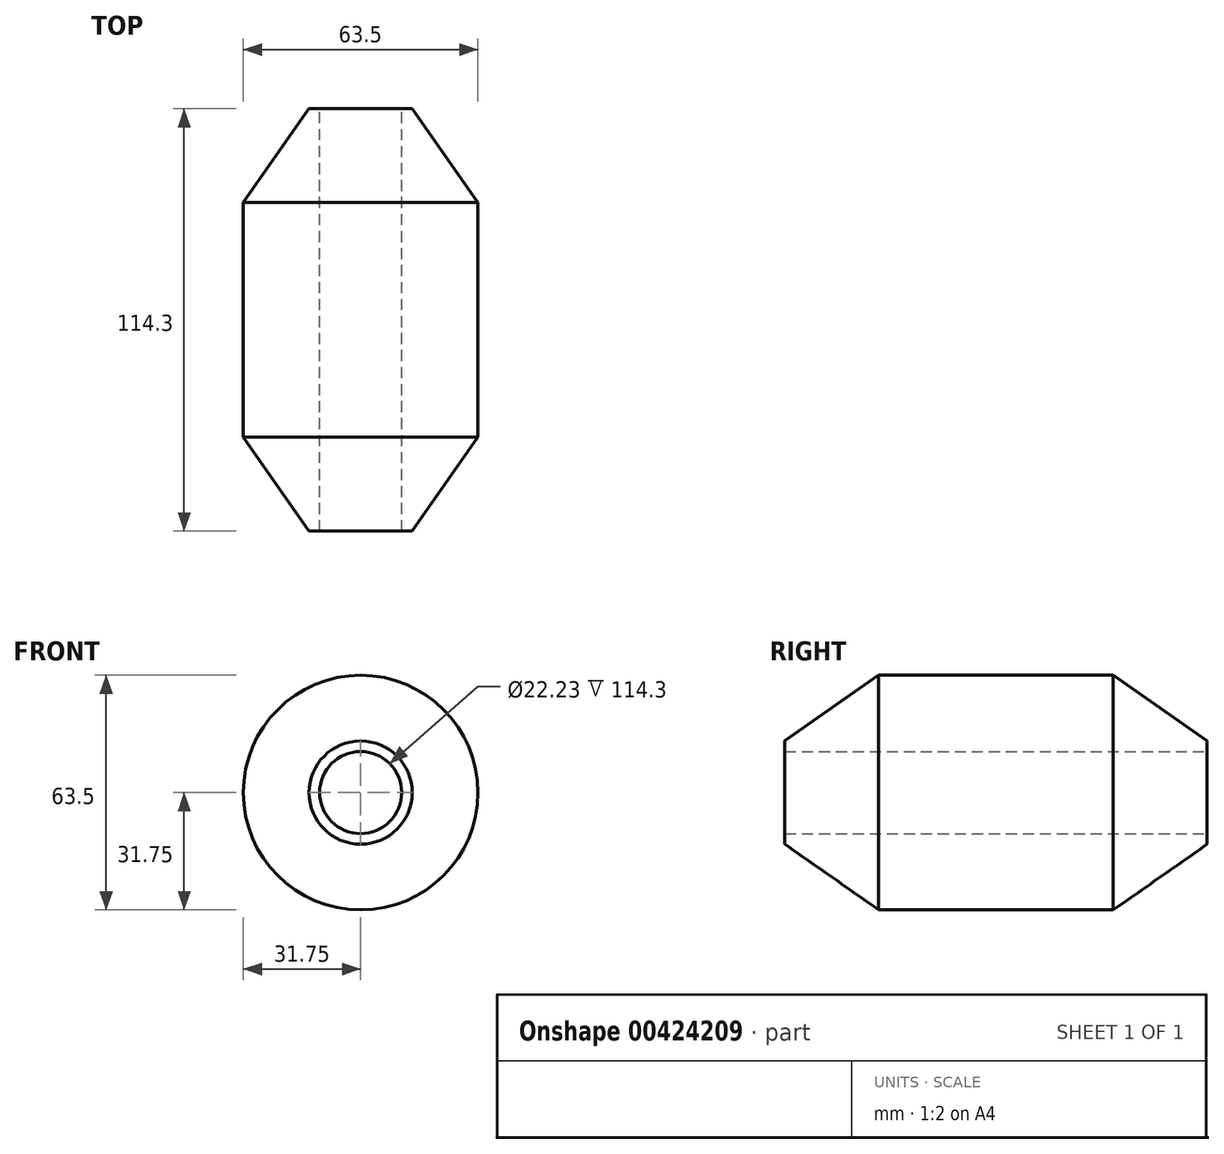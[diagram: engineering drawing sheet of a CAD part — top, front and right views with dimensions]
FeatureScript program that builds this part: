
annotation { "Feature Type Name" : "Feature", "Feature Type Description" : "" }
export const myFeature = defineFeature(function(context is Context, id is Id, definition is map)
    precondition{}
    {
        {
            var Q0;
            Q0=qCreatedBy(makeId("Front.planeOp"),FACE);
            var sketch = newSketch(context, id + "F0", { "sketchPlane" : qUnion([Q0])});
            skCircle(sketch, "E0", {"center": v(0, 0) * mm, "radius": 11.11 * mm});
            skCircle(sketch, "E1", {"center": v(0, 0) * mm, "radius": 31.75 * mm});
            skSolve(sketch);
        }
        {
            var Q0;
            Q0=makeQuery(id+"F0.imprint","IMPRINT",FACE,{"disambiguationData":[TD([[makeQuery(id+"F0.imprint","IMPRINT",EDGE,{"derivedFrom":sQuery(id+"F0.wireOp",EDGE,"E0")}),-1.0]])]});
            extrude(context, id + "F1", {"entities" : qUnion([Q0]), "depth" : 114.3 * mm});
        }
        {
            var Q0;
            Q0=makeQuery(id+"F1.opExtrude","SWEPT_FACE",FACE,{"disambiguationData":[OSD([sQuery(id+"F0.wireOp",EDGE,"E1")])]});
            chamfer(context, id + "F2", {"entities" : qUnion([Q0]), "chamferType" : ChamferType.OFFSET_ANGLE, "width" : 25.4 * mm, "oppositeDirection" : false, "angle" : 35 * degree});
        }
    });
